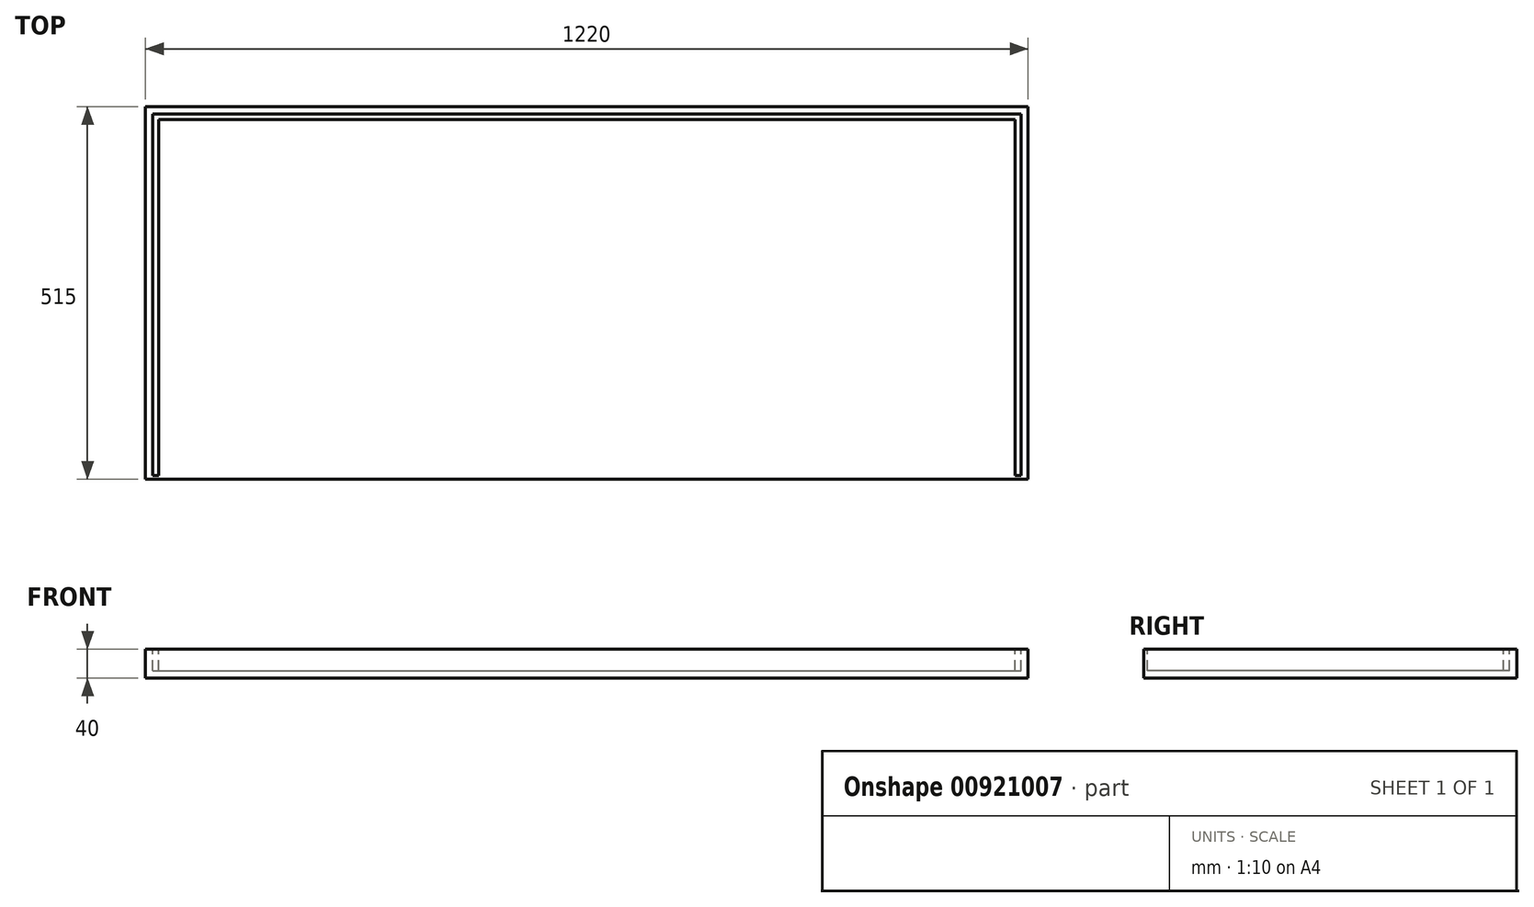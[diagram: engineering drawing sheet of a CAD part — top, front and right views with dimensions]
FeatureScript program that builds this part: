
annotation { "Feature Type Name" : "Feature", "Feature Type Description" : "" }
export const myFeature = defineFeature(function(context is Context, id is Id, definition is map)
    precondition{}
    {
        {
            var Q0;
            Q0=qCreatedBy(makeId("Top.planeOp"),FACE);
            var sketch = newSketch(context, id + "F0", { "sketchPlane" : qUnion([Q0])});
            skLineSegment(sketch, "E0.bottom", {"start": v(-610, 257.5) * mm, "end": v(610, 257.5) * mm});
            skLineSegment(sketch, "E0.top", {"start": v(-610, -257.5) * mm, "end": v(610, -257.5) * mm});
            skLineSegment(sketch, "E0.left", {"start": v(-610, 257.5) * mm, "end": v(-610, -257.5) * mm});
            skLineSegment(sketch, "E0.right", {"start": v(610, 257.5) * mm, "end": v(610, -257.5) * mm});
            skPoint(sketch, "E0.middle", {"position": v(0, 0) * mm});
            skSolve(sketch);
        }
        {
            var Q0;
            Q0=makeQuery(id+"F0.imprint","IMPRINT",FACE,{"disambiguationData":[TD([[makeQuery(id+"F0.imprint","IMPRINT",EDGE,{"derivedFrom":sQuery(id+"F0.wireOp",EDGE,"E0.bottom")}),-1.0]])]});
            extrude(context, id + "F1", {"entities" : qUnion([Q0]), "endBound" : BoundingType.SYMMETRIC, "depth" : 40 * mm, "offsetDistance" : 25 * mm});
        }
        {
            var Q0;
            Q0=makeQuery(id+"F1.opExtrude","CAP_FACE",FACE,{"disambiguationData":[OSD([sQuery(id+"F0.wireOp",EDGE,"E0.bottom"),sQuery(id+"F0.wireOp",EDGE,"E0.top"),sQuery(id+"F0.wireOp",EDGE,"E0.left"),sQuery(id+"F0.wireOp",EDGE,"E0.right")])],"isStart":false});
            var sketch = newSketch(context, id + "F2", { "sketchPlane" : qUnion([Q0])});
            skLineSegment(sketch, "E1.bottom", {"start": v(-600, 247.5) * mm, "end": v(600, 247.5) * mm});
            skLineSegment(sketch, "E1.top", {"start": v(-600, 239.5) * mm, "end": v(600, 239.5) * mm});
            skLineSegment(sketch, "E1.left", {"start": v(-600, 247.5) * mm, "end": v(-600, 239.5) * mm});
            skLineSegment(sketch, "E1.right", {"start": v(600, 247.5) * mm, "end": v(600, 239.5) * mm});
            skSolve(sketch);
        }
        {
            var Q0;
            Q0=qSketchRegion(id+"F2",true);
            extrude(context, id + "F3", {"entities" : qUnion([Q0]), "operationType" : NewBodyOperationType.REMOVE, "oppositeDirection" : true, "depth" : 30 * mm, "offsetDistance" : 25 * mm});
        }
        {
            var Q0;
            Q0=makeQuery(id+"F1.opExtrude","CAP_FACE",FACE,{"disambiguationData":[OSD([sQuery(id+"F0.wireOp",EDGE,"E0.bottom"),sQuery(id+"F0.wireOp",EDGE,"E0.top"),sQuery(id+"F0.wireOp",EDGE,"E0.left"),sQuery(id+"F0.wireOp",EDGE,"E0.right")])],"isStart":false});
            var sketch = newSketch(context, id + "F4", { "sketchPlane" : qUnion([Q0])});
            skLineSegment(sketch, "E2.bottom", {"start": v(-600, 239.5) * mm, "end": v(-592, 239.5) * mm});
            skLineSegment(sketch, "E2.top", {"start": v(-600, -252.5) * mm, "end": v(-592, -252.5) * mm});
            skLineSegment(sketch, "E2.left", {"start": v(-600, 239.5) * mm, "end": v(-600, -252.5) * mm});
            skLineSegment(sketch, "E2.right", {"start": v(-592, 239.5) * mm, "end": v(-592, -252.5) * mm});
            skSolve(sketch);
        }
        {
            var Q0;
            Q0=qSketchRegion(id+"F4",true);
            extrude(context, id + "F5", {"entities" : qUnion([Q0]), "operationType" : NewBodyOperationType.REMOVE, "oppositeDirection" : true, "depth" : 30 * mm, "offsetDistance" : 25 * mm});
        }
        {
            var Q0;
            Q0=makeQuery(id+"F1.opExtrude","CAP_FACE",FACE,{"disambiguationData":[OSD([sQuery(id+"F0.wireOp",EDGE,"E0.bottom"),sQuery(id+"F0.wireOp",EDGE,"E0.top"),sQuery(id+"F0.wireOp",EDGE,"E0.left"),sQuery(id+"F0.wireOp",EDGE,"E0.right")])],"isStart":false});
            var sketch = newSketch(context, id + "F6", { "sketchPlane" : qUnion([Q0])});
            skLineSegment(sketch, "E3.bottom", {"start": v(592, 239.5) * mm, "end": v(600, 239.5) * mm});
            skLineSegment(sketch, "E3.top", {"start": v(592, -252.5) * mm, "end": v(600, -252.5) * mm});
            skLineSegment(sketch, "E3.left", {"start": v(592, 239.5) * mm, "end": v(592, -252.5) * mm});
            skLineSegment(sketch, "E3.right", {"start": v(600, 239.5) * mm, "end": v(600, -252.5) * mm});
            skSolve(sketch);
        }
        {
            var Q0;
            Q0=makeQuery(id+"F6.imprint","IMPRINT",FACE,{"disambiguationData":[TD([[makeQuery(id+"F6.imprint","IMPRINT",EDGE,{"derivedFrom":sQuery(id+"F6.wireOp",EDGE,"E3.bottom")}),-1.0]])]});
            extrude(context, id + "F7", {"entities" : qUnion([Q0]), "operationType" : NewBodyOperationType.REMOVE, "oppositeDirection" : true, "depth" : 30 * mm, "offsetDistance" : 25 * mm});
        }
    });
